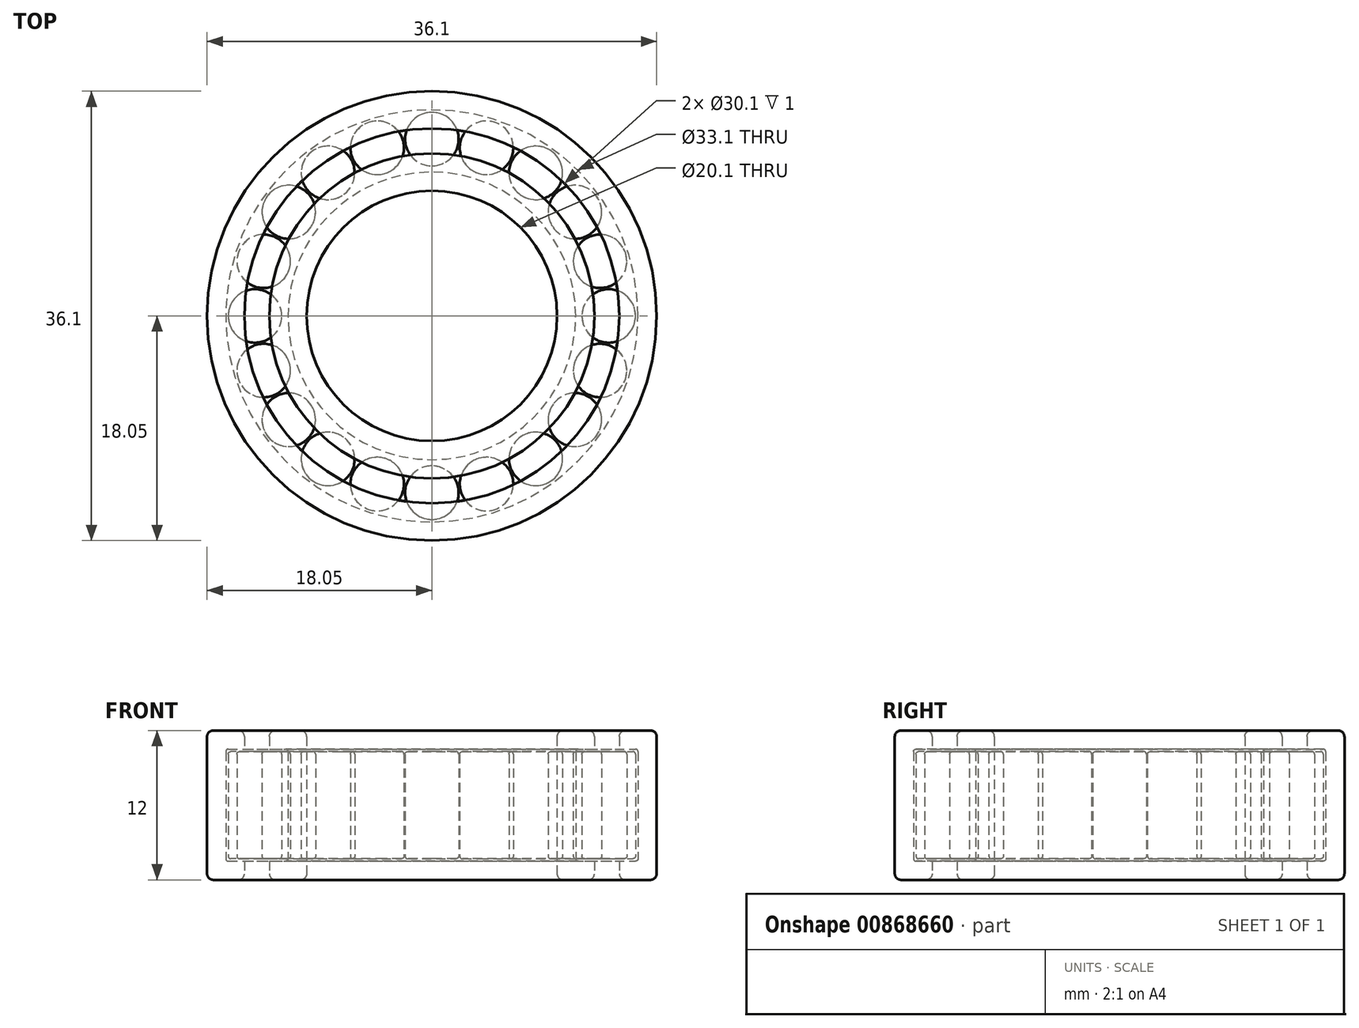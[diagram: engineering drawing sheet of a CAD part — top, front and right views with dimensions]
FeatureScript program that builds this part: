
annotation { "Feature Type Name" : "Feature", "Feature Type Description" : "" }
export const myFeature = defineFeature(function(context is Context, id is Id, definition is map)
    precondition{}
    {
        {
            var Q0;
            Q0=qCreatedBy(makeId("Front.planeOp"),FACE);
            var sketch = newSketch(context, id + "F0", { "sketchPlane" : qUnion([Q0])});
            skLineSegment(sketch, "E0", {"start": v(0, -11.2) * mm, "end": v(0, 11.2) * mm, "construction": true});
            skLineSegment(sketch, "E1.bottom", {"start": v(-15.05, 0) * mm, "end": v(-18.05, 0) * mm});
            skLineSegment(sketch, "E1.top", {"start": v(-15.05, 12) * mm, "end": v(-18.05, 12) * mm});
            skLineSegment(sketch, "E1.left", {"start": v(-15.05, 0) * mm, "end": v(-15.05, 1.5) * mm});
            skLineSegment(sketch, "E1.right", {"start": v(-18.05, 0) * mm, "end": v(-18.05, 12) * mm});
            skLineSegment(sketch, "E2.bottom", {"start": v(-15.05, 10.5) * mm, "end": v(-16.55, 10.5) * mm});
            skLineSegment(sketch, "E2.top", {"start": v(-15.05, 1.5) * mm, "end": v(-16.55, 1.5) * mm});
            skLineSegment(sketch, "E2.right", {"start": v(-16.55, 10.5) * mm, "end": v(-16.55, 1.5) * mm});
            skLineSegment(sketch, "E3.trimOffspring", {"start": v(-15.05, 10.5) * mm, "end": v(-15.05, 12) * mm});
            skLineSegment(sketch, "E4", {"start": v(-14.05, -5.04) * mm, "end": v(-14.05, 20.1) * mm, "construction": true});
            skLineSegment(sketch, "E5.MirrorCS", {"start": v(-13.05, 12) * mm, "end": v(-10.05, 12) * mm});
            skLineSegment(sketch, "E6.MirrorCS", {"start": v(-13.05, 10.5) * mm, "end": v(-13.05, 12) * mm});
            skLineSegment(sketch, "E7.MirrorCS", {"start": v(-13.05, 10.5) * mm, "end": v(-11.55, 10.5) * mm});
            skLineSegment(sketch, "E8.MirrorCS", {"start": v(-11.55, 10.5) * mm, "end": v(-11.55, 1.5) * mm});
            skLineSegment(sketch, "E9.MirrorCS", {"start": v(-10.05, 0) * mm, "end": v(-10.05, 12) * mm});
            skLineSegment(sketch, "E10.MirrorCS", {"start": v(-13.05, 0) * mm, "end": v(-10.05, 0) * mm});
            skLineSegment(sketch, "E11.MirrorCS", {"start": v(-13.05, 0) * mm, "end": v(-13.05, 1.5) * mm});
            skLineSegment(sketch, "E12.MirrorCS", {"start": v(-13.05, 1.5) * mm, "end": v(-11.55, 1.5) * mm});
            skSolve(sketch);
        }
        {
            var Q0;
            Q0=qSketchRegion(id+"F0",true);
            var Q1;
            Q1=sQuery(id+"F0.wireOp",EDGE,"E0");
            revolve(context, id + "F1", {"surfaceOperationType" : NewSurfaceOperationType.NEW, "entities" : qUnion([Q0]), "axis" : qUnion([Q1]), "revolveType" : RevolveType.FULL});
        }
        {
            var Q0;
            Q0=makeQuery(id+"F1.opRevolve","SWEPT_FACE",FACE,{"disambiguationData":[OSD([sQuery(id+"F0.wireOp",EDGE,"E2.top")])]});
            cPlane(context, id + "F2", {"entities" : qUnion([Q0]), "cplaneType" : CPlaneType.OFFSET, "offset" : 0.2 * mm, "width" : 150 * mm, "height" : 150 * mm});
        }
        {
            var Q0;
            Q0=qCreatedBy(id+"F2.planeOp",FACE);
            var sketch = newSketch(context, id + "F3", { "sketchPlane" : qUnion([Q0])});
            skCircle(sketch, "E13", {"center": v(-14.2, 0) * mm, "radius": 2.15 * mm});
            skSolve(sketch);
        }
        {
            var Q0;
            Q0=qSketchRegion(id+"F3",true);
            var Q1;
            Q1=makeQuery(id+"F1.opRevolve","SWEPT_FACE",FACE,{"disambiguationData":[OSD([sQuery(id+"F0.wireOp",EDGE,"E2.bottom")])]});
            extrude(context, id + "F4", {"entities" : qUnion([Q0]), "flatOperationType" : FlatOperationType.REMOVE, "depth" : 8.6 * mm, "endBoundEntityFace" : qUnion([Q1]), "offsetDistance" : 25 * mm, "domain" : OperationDomain.MODEL});
        }
        {
            var Q0;
            Q0=makeQuery(id+"F1.opRevolve","SWEPT_FACE",FACE,{"disambiguationData":[OSD([sQuery(id+"F0.wireOp",EDGE,"E1.top")])]});
            var Q1;
            Q1=makeQuery(id+"F1.opRevolve","SWEPT_FACE",FACE,{"disambiguationData":[OSD([sQuery(id+"F0.wireOp",EDGE,"E5.MirrorCS")])]});
            var Q2;
            Q2=makeQuery(id+"F1.opRevolve","SWEPT_FACE",FACE,{"disambiguationData":[OSD([sQuery(id+"F0.wireOp",EDGE,"E1.bottom")])]});
            var Q3;
            Q3=makeQuery(id+"F1.opRevolve","SWEPT_FACE",FACE,{"disambiguationData":[OSD([sQuery(id+"F0.wireOp",EDGE,"E10.MirrorCS")])]});
            fillet(context, id + "F5", {"entities" : qUnion([Q0, Q1, Q2, Q3]), "radius" : .5 * mm, "tangentPropagation" : true, "allowEdgeOverflow" : false});
        }
        {
            var Q0;
            Q0=makeQuery(id+"F1.opRevolve","SWEPT_FACE",FACE,{"disambiguationData":[OSD([sQuery(id+"F0.wireOp",EDGE,"E2.right")])]});
            var Q1;
            Q1=makeQuery(id+"F4.opExtrude","SWEPT_FACE",FACE,{"disambiguationData":[OSD([sQuery(id+"F3.wireOp",EDGE,"E13")])]});
            var Q2;
            Q2=makeQuery(id+"F1.opRevolve","SWEPT_FACE",FACE,{"disambiguationData":[OSD([sQuery(id+"F0.wireOp",EDGE,"E8.MirrorCS")])]});
            fillet(context, id + "F6", {"entities" : qUnion([Q0, Q1, Q2]), "radius" : .2 * mm, "tangentPropagation" : true, "allowEdgeOverflow" : false});
        }
        {
            var Q0;
            Q0=makeQuery(id+"F4.opExtrude","SWEPT_BODY",BODY,{"disambiguationData":[OSD([sQuery(id+"F3.wireOp",EDGE,"E13")])]});
            var Q1;
            Q1=sQuery(id+"F0.wireOp",EDGE,"E0");
            circularPattern(context, id + "F7", {"entities" : qUnion([Q0]), "axis" : qUnion([Q1]), "angle" : 360 * degree, "instanceCount" : 20, "equalSpace" : true, "fullFeaturePattern" : false});
        }
    });
